# Revit family: Table-LAMMHULTS-COOPER-High
name_source: partatom
category: Furniture
revit_build: Autodesk Revit 2015 (Build: 20160512_0715(x64)
units: mm (PartAtom-declared; Revit-internal decimal feet)

## types (2) — shared parameters
Assembly Code = E2020
Description = *Please enter mtrl description here for use in mto*
Feet Material = Metal - Chrome - Polished
Frame Material = Metal - Chrome - Polished
Keynote = 46.B
Leg Width = 284 mm
Legs Material = Metal - Chrome - Polished
Manufacturer = LAMMHULTS
Model = COOPER
Table Edge Material = <By Category>
Table Top Height = 1046 mm  [stored 3.43176 ft]
Table Top Material = Laminate - High Pressure - White grey
Table Top Width = 600 mm  [stored 1.9685 ft]
URL = www.lammhults.se

## per-type parameters (varying)
| type | Table Top Length |
| 160x60 Laminate | 1600 mm  [stored 5.24934 ft] |
| 200x60 Laminate | 2000 mm  [stored 6.56168 ft] |

note: [stored X ft] marks values corroborated as IEEE doubles in the binary element streams (Revit-internal decimal feet)

## geometry (parser evidence)
native form markers: Blend x10, Sweep x2
no freeform markers — native parametric forms only
